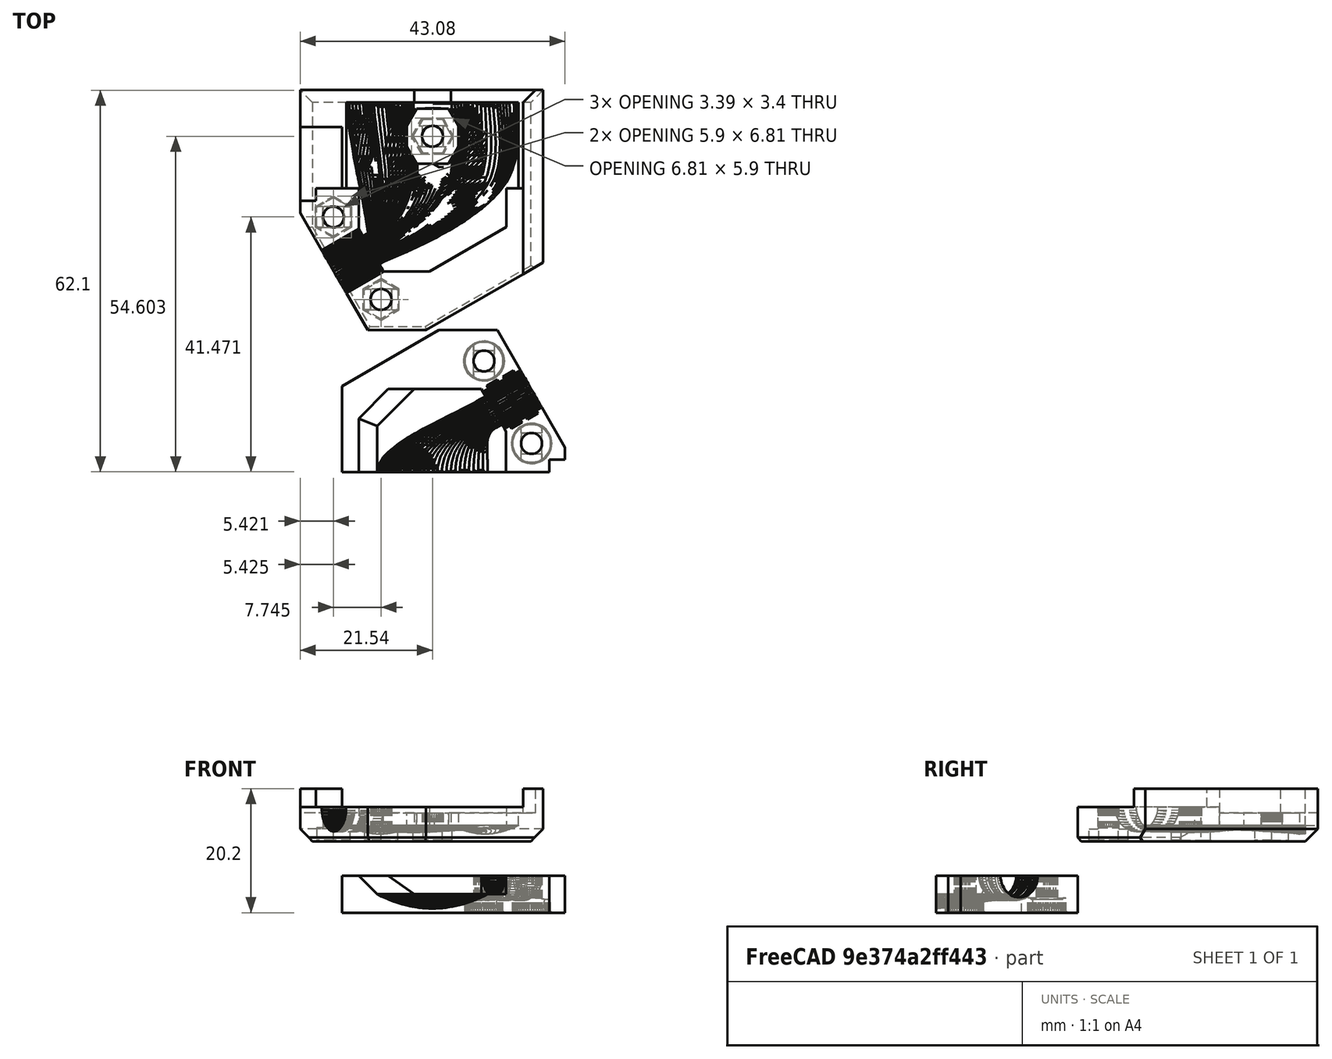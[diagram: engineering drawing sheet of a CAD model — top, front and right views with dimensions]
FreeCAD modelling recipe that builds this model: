
FCSTD DOCUMENT  (FreeCAD 0.18R16146 (Git))
Label: min-bed-wire-mounter
License: All rights reserved
LicenseURL: http://en.wikipedia.org/wiki/All_rights_reserved
objects: Part::Feature×8, Mesh::Feature×2, Part::Mirroring×2, Part::Box×1, Part::Cut×1
note: 12 computed .brp shape members not serialized (recipe doc carries the construction recipe); baked Part::Feature solids carry a one-line shape summary decoded from their .brp

FEATURE [Mesh::Feature] Top
FEATURE [Part::Feature] Top001
  shape: bbox 39.54 x 39.05 x 8.6 mm, 5096 faces, 0 solids (baked)
FEATURE [Part::Feature] Top001001  label="Top002"
  shape: bbox 39.54 x 39.05 x 8.6 mm, 4570 faces, 0 solids (baked)
FEATURE [Part::Box] Box  label="Cube"
  AttacherType = Attacher::AttachEngine3D
  Height = 10
  Length = 10
  Placement = pos=(14,33.05,4.6) rot=(0,0,1;0rad)
  Width = 10
FEATURE [Part::Feature] Top001001_solid  label="Top002 (Solid)"
  shape: bbox 39.54 x 39.05 x 8.6 mm, 4570 faces (baked)
FEATURE [Part::Cut] Cut
  Base = -> Top001001_solid
  Tool = -> Box
FEATURE [Part::Mirroring] Part__Mirroring  label="Cut (Mirror #1)"
  Base = (0,0,0)
  Normal = (1,0,0)
  Source = -> Cut
FEATURE [Part::Feature] Part__Mirroring001  label="top"
  shape: bbox 39.54 x 39.05 x 8.6 mm, 4569 faces (baked)
FEATURE [Mesh::Feature] Bottom
FEATURE [Part::Feature] Bottom001
  shape: bbox 36.29 x 23.05 x 6 mm, 3262 faces, 0 solids (baked)
FEATURE [Part::Feature] Bottom001001  label="Bottom002"
  shape: bbox 36.29 x 23.05 x 6 mm, 2673 faces, 0 solids (baked)
FEATURE [Part::Feature] Bottom001001_solid  label="Bottom002 (Solid)"
  shape: bbox 36.29 x 23.05 x 6 mm, 2673 faces (baked)
FEATURE [Part::Mirroring] Part__Mirroring002  label="Bottom002 (Mirror #2)"
  Base = (0,0,0)
  Normal = (1,0,0)
  Source = -> Bottom001001
FEATURE [Part::Feature] Part__Mirroring002001  label="bottom"
  shape: bbox 36.29 x 23.05 x 6 mm, 2673 faces, 0 solids (baked)
